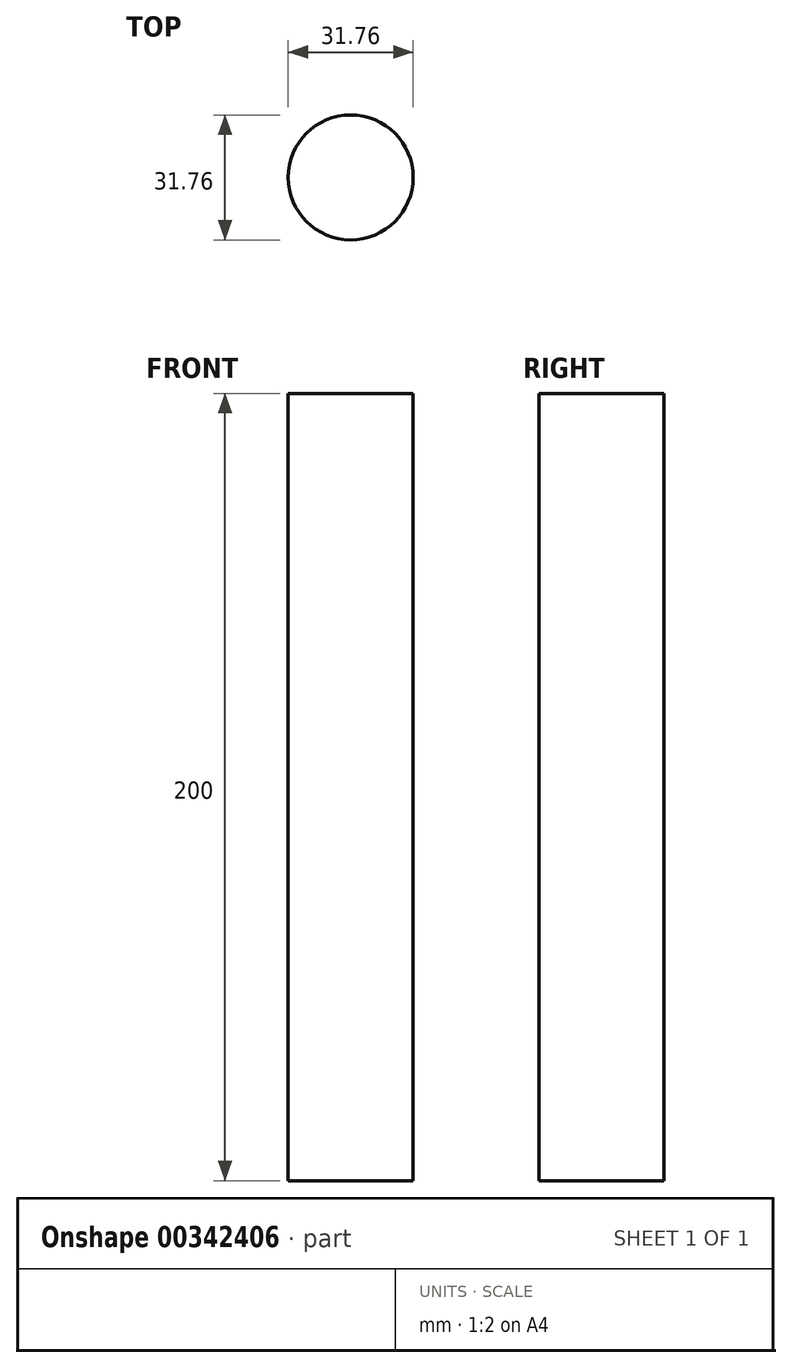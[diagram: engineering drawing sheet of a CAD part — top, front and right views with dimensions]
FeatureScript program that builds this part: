
annotation { "Feature Type Name" : "Feature", "Feature Type Description" : "" }
export const myFeature = defineFeature(function(context is Context, id is Id, definition is map)
    precondition{}
    {
        {
            var Q0;
            Q0=qCreatedBy(makeId("Top.planeOp"),FACE);
            var sketch = newSketch(context, id + "F0", { "sketchPlane" : qUnion([Q0])});
            skCircle(sketch, "E0", {"center": v(0, 0) * mm, "radius": 15.88 * mm});
            skSolve(sketch);
        }
        {
            var Q0;
            Q0 = qSketchRegion(id + "F0", true);
            extrude(context, id + "F1", {"entities" : qUnion([Q0]), "endBound" : BoundingType.SYMMETRIC, "depth" : 200 * mm});
        }
    });
